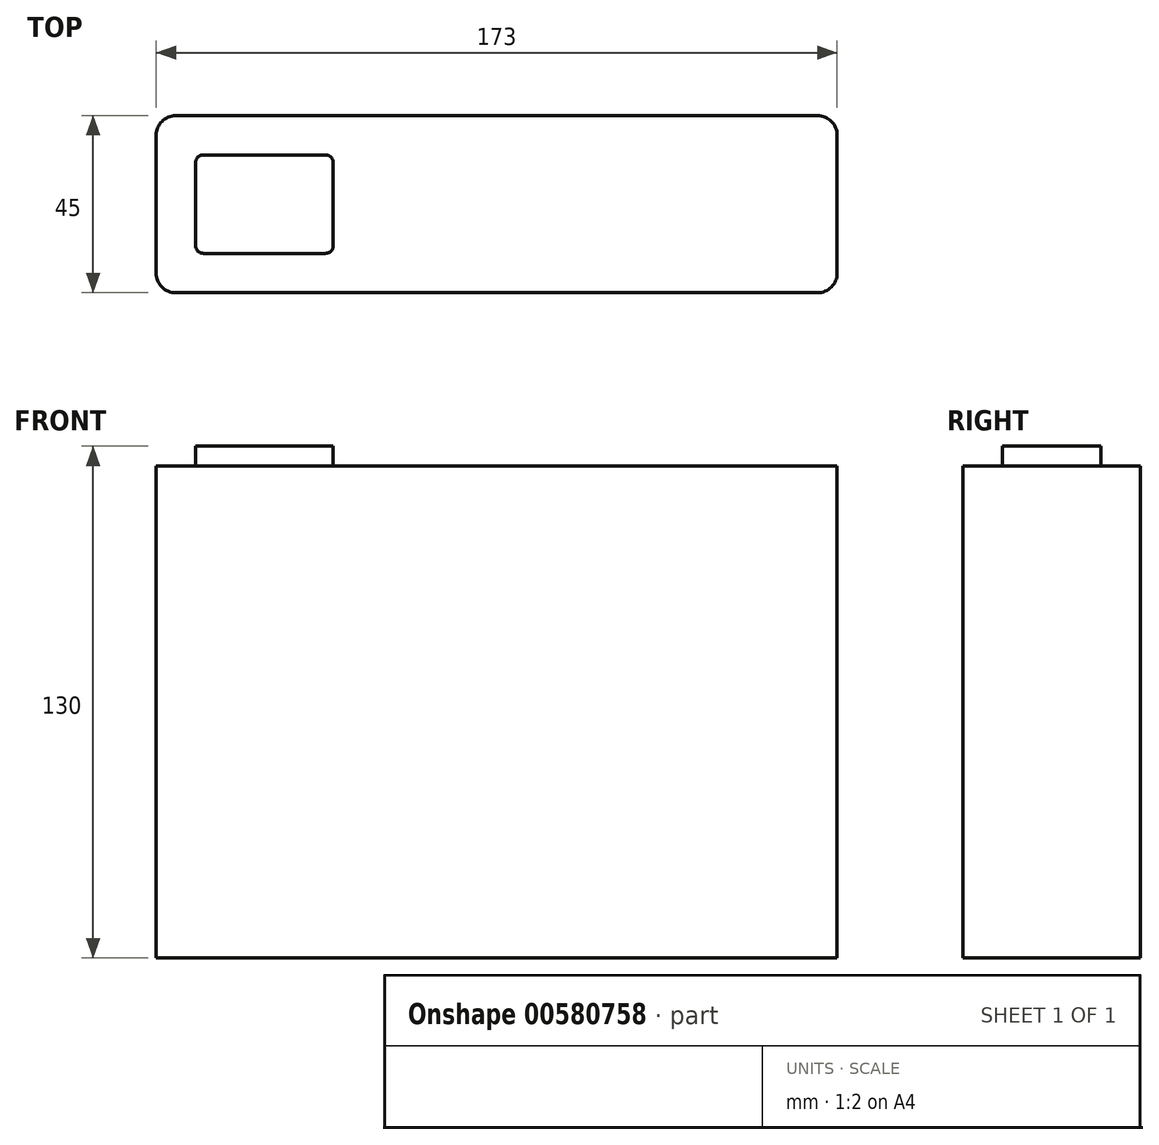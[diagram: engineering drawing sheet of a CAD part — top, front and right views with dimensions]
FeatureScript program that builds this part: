
annotation { "Feature Type Name" : "Feature", "Feature Type Description" : "" }
export const myFeature = defineFeature(function(context is Context, id is Id, definition is map)
    precondition{}
    {
        {
            var Q0;
            Q0=qCreatedBy(makeId("Front.planeOp"),FACE);
            var sketch = newSketch(context, id + "F0", { "sketchPlane" : qUnion([Q0])});
            skLineSegment(sketch, "E0.bottom", {"start": v(0, 0) * mm, "end": v(-173, 0) * mm});
            skLineSegment(sketch, "E0.top", {"start": v(0, 125) * mm, "end": v(-173, 125) * mm});
            skLineSegment(sketch, "E0.left", {"start": v(0, 0) * mm, "end": v(0, 125) * mm});
            skLineSegment(sketch, "E0.right", {"start": v(-173, 0) * mm, "end": v(-173, 125) * mm});
            skSolve(sketch);
        }
        {
            var Q0;
            Q0 = qSketchRegion(id + "F0", true);
            extrude(context, id + "F1", {"entities" : qUnion([Q0]), "oppositeDirection" : true, "depth" : 45 * mm, "offsetDistance" : 25 * mm});
        }
        {
            var Q0;
            Q0=makeQuery(id+"F1.opExtrude","CAP_EDGE",EDGE,{"disambiguationData":[OSD([sQuery(id+"F0.wireOp",EDGE,"E0.left")])],"isStart":true});
            fillet(context, id + "F2", {"entities" : qUnion([Q0]), "radius" : 5 * mm, "tangentPropagation" : true, "allowEdgeOverflow" : false});
        }
        {
            var Q0;
            Q0=makeQuery(id+"F1.opExtrude","CAP_EDGE",EDGE,{"disambiguationData":[OSD([sQuery(id+"F0.wireOp",EDGE,"E0.left")])],"isStart":false});
            var Q1;
            Q1=makeQuery(id+"F1.opExtrude","CAP_EDGE",EDGE,{"disambiguationData":[OSD([sQuery(id+"F0.wireOp",EDGE,"E0.right")])],"isStart":false});
            var Q2;
            Q2=makeQuery(id+"F1.opExtrude","CAP_EDGE",EDGE,{"disambiguationData":[OSD([sQuery(id+"F0.wireOp",EDGE,"E0.right")])],"isStart":true});
            fillet(context, id + "F3", {"entities" : qUnion([Q0, Q1, Q2]), "radius" : 5 * mm, "tangentPropagation" : true, "allowEdgeOverflow" : false});
        }
        {
            var Q0;
            Q0=makeQuery(id+"F1.opExtrude","SWEPT_FACE",FACE,{"disambiguationData":[OSD([sQuery(id+"F0.wireOp",EDGE,"E0.top")])]});
            var sketch = newSketch(context, id + "F4", { "sketchPlane" : qUnion([Q0])});
            skLineSegment(sketch, "E1.bottom", {"start": v(-161, 35) * mm, "end": v(-130, 35) * mm});
            skLineSegment(sketch, "E1.top", {"start": v(-161, 10) * mm, "end": v(-130, 10) * mm});
            skLineSegment(sketch, "E1.left", {"start": v(-163, 33) * mm, "end": v(-163, 12) * mm});
            skLineSegment(sketch, "E1.right", {"start": v(-128, 33) * mm, "end": v(-128, 12) * mm});
            skPoint(sketch, "E2.visualSharp", {"position": v(-163, 35) * mm});
            skArc(sketch, "E2.filletArc", {"start": v(-161, 35) * mm, "mid": v(-162.41, 34.41) * mm, "end": v(-163, 33) * mm});
            skPoint(sketch, "E3.visualSharp", {"position": v(-128, 35) * mm});
            skArc(sketch, "E3.filletArc", {"start": v(-128, 33) * mm, "mid": v(-128.59, 34.41) * mm, "end": v(-130, 35) * mm});
            skPoint(sketch, "E4.visualSharp", {"position": v(-128, 10) * mm});
            skArc(sketch, "E4.filletArc", {"start": v(-130, 10) * mm, "mid": v(-128.59, 10.59) * mm, "end": v(-128, 12) * mm});
            skPoint(sketch, "E5.visualSharp", {"position": v(-163, 10) * mm});
            skArc(sketch, "E5.filletArc", {"start": v(-163, 12) * mm, "mid": v(-162.41, 10.59) * mm, "end": v(-161, 10) * mm});
            skSolve(sketch);
        }
        {
            var Q0;
            Q0 = qSketchRegion(id + "F4", true);
            extrude(context, id + "F5", {"entities" : qUnion([Q0]), "operationType" : NewBodyOperationType.ADD, "depth" : 5 * mm, "offsetDistance" : 25 * mm});
        }
        {
            var Q0;
            Q0=makeQuery(id+"F1.opExtrude","CAP_EDGE",EDGE,{"disambiguationData":[OSD([sQuery(id+"F0.wireOp",EDGE,"E0.top")])],"isStart":true});
            cPoint(context, id + "F6", {"entities" : qUnion([Q0]), "parameter" : 0.5});
        }
        {
            var Q0;
            Q0=makeQuery(id+"F1.opExtrude","CAP_EDGE",EDGE,{"disambiguationData":[OSD([sQuery(id+"F0.wireOp",EDGE,"E0.top")])],"isStart":false});
            cPoint(context, id + "F7", {"entities" : qUnion([Q0]), "parameter" : 0.5});
        }
        {
            var Q0;
            Q0=makeQuery(id+"F1.opExtrude","CAP_EDGE",EDGE,{"disambiguationData":[OSD([sQuery(id+"F0.wireOp",EDGE,"E0.bottom")])],"isStart":true});
            cPoint(context, id + "F8", {"entities" : qUnion([Q0]), "parameter" : 0.5});
        }
        {
            var Q0;
            Q0 = qCreatedBy(id + "F6" ,VERTEX);
            var Q1;
            Q1 = qCreatedBy(id + "F7" ,VERTEX);
            var Q2;
            Q2 = qCreatedBy(id + "F8" ,VERTEX);
            cPlane(context, id + "F9", {"entities" : qUnion([Q0, Q1, Q2]), "cplaneType" : CPlaneType.THREE_POINT, "offset" : 25 * mm, "width" : 150 * mm, "height" : 150 * mm});
        }
    });
